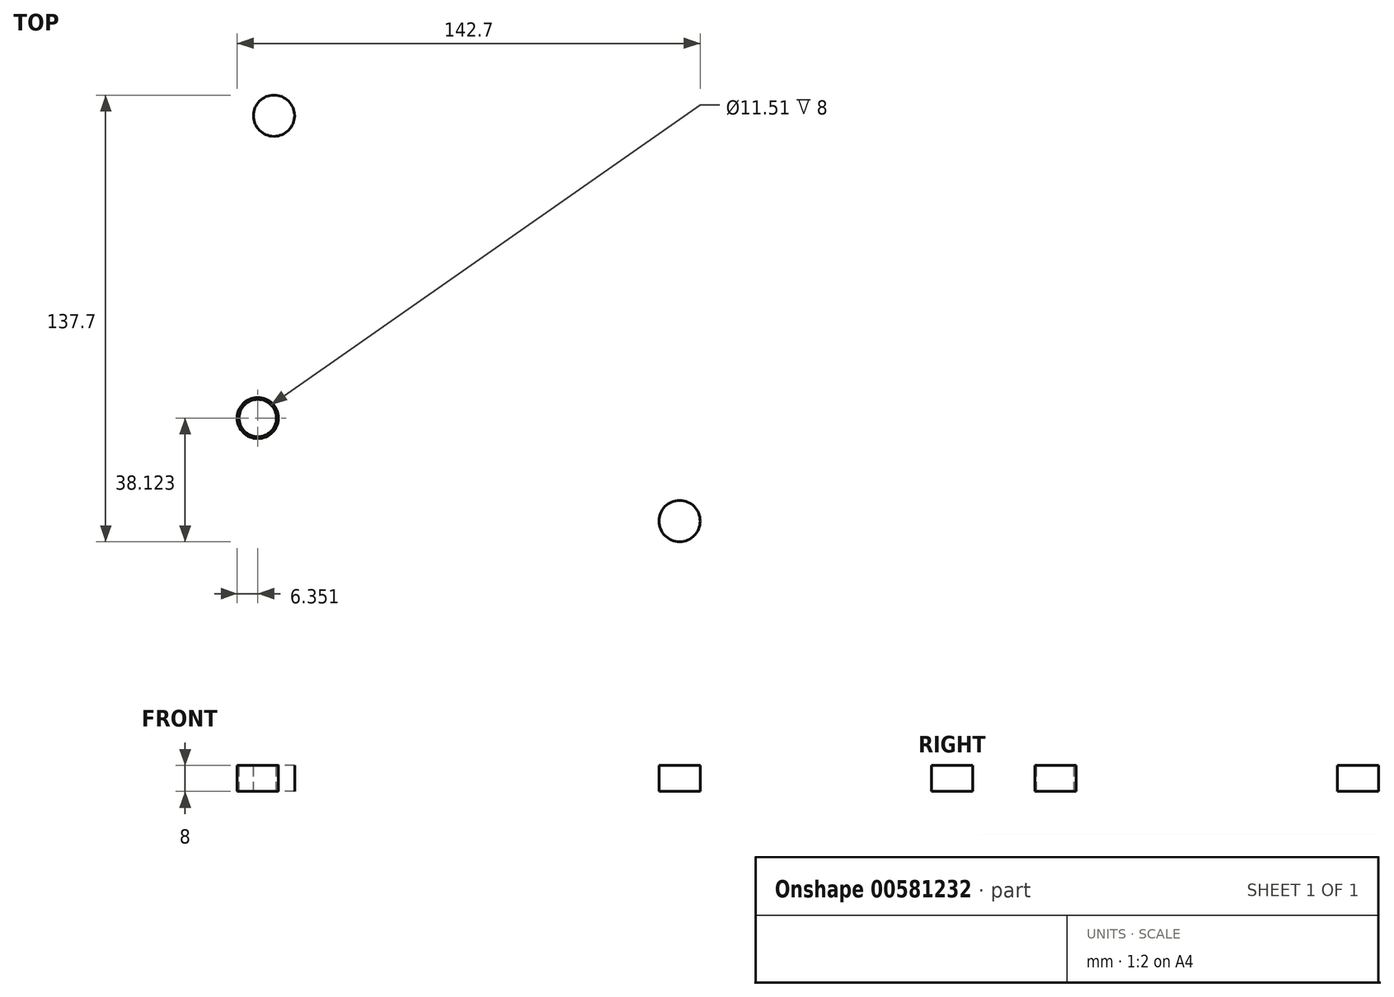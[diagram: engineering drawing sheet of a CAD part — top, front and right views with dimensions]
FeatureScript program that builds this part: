
annotation { "Feature Type Name" : "Feature", "Feature Type Description" : "" }
export const myFeature = defineFeature(function(context is Context, id is Id, definition is map)
    precondition{}
    {
        {
            var Q0;
            Q0=qCreatedBy(makeId("Top.planeOp"),FACE);
            var sketch = newSketch(context, id + "F0", { "sketchPlane" : qUnion([Q0])});
            skLineSegment(sketch, "E0.bottom", {"start": v(-93.63, 124.58) * mm, "end": v(31.37, 124.58) * mm});
            skLineSegment(sketch, "E0.top", {"start": v(-93.63, -40.42) * mm, "end": v(31.37, -40.42) * mm});
            skLineSegment(sketch, "E0.left", {"start": v(-113.63, 104.58) * mm, "end": v(-113.63, -20.42) * mm});
            skLineSegment(sketch, "E0.right", {"start": v(51.37, 104.58) * mm, "end": v(51.37, -20.42) * mm});
            skPoint(sketch, "E1.visualSharp", {"position": v(-113.63, 124.58) * mm});
            skArc(sketch, "E1.filletArc", {"start": v(-93.63, 124.58) * mm, "mid": v(-107.77, 118.73) * mm, "end": v(-113.63, 104.58) * mm});
            skPoint(sketch, "E2.visualSharp", {"position": v(51.37, 124.58) * mm});
            skArc(sketch, "E2.filletArc", {"start": v(51.37, 104.58) * mm, "mid": v(45.51, 118.73) * mm, "end": v(31.37, 124.58) * mm});
            skPoint(sketch, "E3.visualSharp", {"position": v(51.37, -40.42) * mm});
            skArc(sketch, "E3.filletArc", {"start": v(31.37, -40.42) * mm, "mid": v(45.51, -34.56) * mm, "end": v(51.37, -20.42) * mm});
            skPoint(sketch, "E4.visualSharp", {"position": v(-113.63, -40.42) * mm});
            skArc(sketch, "E4.filletArc", {"start": v(-113.63, -20.42) * mm, "mid": v(-107.77, -34.56) * mm, "end": v(-93.63, -40.42) * mm});
            skLineSegment(sketch, "E5.0", {"start": v(-68.63, 94.58) * mm, "end": v(6.37, 94.58) * mm});
            skLineSegment(sketch, "E5.1", {"start": v(-83.63, 79.58) * mm, "end": v(-83.63, 4.58) * mm});
            skLineSegment(sketch, "E5.2", {"start": v(-68.63, -10.42) * mm, "end": v(6.37, -10.42) * mm});
            skLineSegment(sketch, "E5.3", {"start": v(21.37, 79.58) * mm, "end": v(21.37, 4.58) * mm});
            skPoint(sketch, "E6.visualSharp", {"position": v(21.37, 94.58) * mm});
            skArc(sketch, "E6.filletArc", {"start": v(21.37, 79.58) * mm, "mid": v(16.98, 90.2) * mm, "end": v(6.37, 94.58) * mm});
            skPoint(sketch, "E7.visualSharp", {"position": v(21.37, -10.42) * mm});
            skArc(sketch, "E7.filletArc", {"start": v(6.37, -10.42) * mm, "mid": v(16.98, -6.02) * mm, "end": v(21.37, 4.58) * mm});
            skPoint(sketch, "E8.visualSharp", {"position": v(-83.63, -10.42) * mm});
            skArc(sketch, "E8.filletArc", {"start": v(-83.63, 4.58) * mm, "mid": v(-79.24, -6.02) * mm, "end": v(-68.63, -10.42) * mm});
            skPoint(sketch, "E9.visualSharp", {"position": v(-83.63, 94.58) * mm});
            skArc(sketch, "E9.filletArc", {"start": v(-68.63, 94.58) * mm, "mid": v(-79.24, 90.2) * mm, "end": v(-83.63, 79.58) * mm});
            skSolve(sketch);
        }
        {
            var Q0;
            Q0=makeQuery(id+"F0.imprint","IMPRINT",FACE,{"disambiguationData":[TD([[makeQuery(id+"F0.imprint","IMPRINT",EDGE,{"derivedFrom":sQuery(id+"F0.wireOp",EDGE,"E0.bottom")}),-1.0]])]});
            extrude(context, id + "F1", {"entities" : qUnion([Q0]), "depth" : 8 * mm, "offsetDistance" : 25 * mm});
        }
        {
            var Q0;
            Q0=makeQuery(id+"F1.opExtrude","CAP_FACE",FACE,{"disambiguationData":[OSD([sQuery(id+"F0.wireOp",EDGE,"E0.bottom"),sQuery(id+"F0.wireOp",EDGE,"E0.top"),sQuery(id+"F0.wireOp",EDGE,"E0.left"),sQuery(id+"F0.wireOp",EDGE,"E0.right"),sQuery(id+"F0.wireOp",EDGE,"E1.filletArc"),sQuery(id+"F0.wireOp",EDGE,"E2.filletArc"),sQuery(id+"F0.wireOp",EDGE,"E3.filletArc"),sQuery(id+"F0.wireOp",EDGE,"E4.filletArc"),sQuery(id+"F0.wireOp",EDGE,"E5.0"),sQuery(id+"F0.wireOp",EDGE,"E5.1"),sQuery(id+"F0.wireOp",EDGE,"E5.2"),sQuery(id+"F0.wireOp",EDGE,"E5.3"),sQuery(id+"F0.wireOp",EDGE,"E6.filletArc"),sQuery(id+"F0.wireOp",EDGE,"E7.filletArc"),sQuery(id+"F0.wireOp",EDGE,"E8.filletArc"),sQuery(id+"F0.wireOp",EDGE,"E9.filletArc")])],"isStart":false});
            var sketch = newSketch(context, id + "F2", { "sketchPlane" : qUnion([Q0])});
            skLineSegment(sketch, "E10", {"start": v(-113.63, 42.08) * mm, "end": v(-83.63, 42.08) * mm, "construction": true});
            skLineSegment(sketch, "E11", {"start": v(-31.13, 124.58) * mm, "end": v(-31.13, 94.58) * mm, "construction": true});
            skLineSegment(sketch, "E12", {"start": v(21.37, 42.08) * mm, "end": v(51.37, 42.08) * mm, "construction": true});
            skLineSegment(sketch, "E13", {"start": v(-31.13, -10.42) * mm, "end": v(-31.13, -40.42) * mm, "construction": true});
            skLineSegment(sketch, "E14", {"start": v(-31.13, -25.42) * mm, "end": v(85, -25.42) * mm, "construction": true});
            skLineSegment(sketch, "E15", {"start": v(-31.13, -25.42) * mm, "end": v(-152.16, -25.42) * mm, "construction": true});
            skLineSegment(sketch, "E16", {"start": v(-31.13, 109.58) * mm, "end": v(69.21, 109.58) * mm, "construction": true});
            skLineSegment(sketch, "E17", {"start": v(-31.13, 109.58) * mm, "end": v(-134.7, 109.58) * mm, "construction": true});
            skLineSegment(sketch, "E18", {"start": v(-98.63, 42.08) * mm, "end": v(-98.63, 145.3) * mm, "construction": true});
            skLineSegment(sketch, "E19", {"start": v(36.37, 42.08) * mm, "end": v(36.37, 143.63) * mm, "construction": true});
            skLineSegment(sketch, "E20", {"start": v(36.37, 42.08) * mm, "end": v(36.37, -62.39) * mm, "construction": true});
            skLineSegment(sketch, "E21", {"start": v(-98.63, 42.08) * mm, "end": v(-98.63, -55.69) * mm, "construction": true});
            skCircle(sketch, "E22", {"center": v(-31.13, 109.58) * mm, "radius": 6.35 * mm});
            skCircle(sketch, "E23", {"center": v(-31.13, -25.42) * mm, "radius": 6.35 * mm});
            skCircle(sketch, "E24", {"center": v(-98.63, 42.08) * mm, "radius": 6.35 * mm});
            skCircle(sketch, "E25", {"center": v(36.37, 42.08) * mm, "radius": 6.35 * mm});
            skCircle(sketch, "E26", {"center": v(31.37, 104.58) * mm, "radius": 6.35 * mm});
            skCircle(sketch, "E27.MirrorC", {"center": v(31.37, -20.42) * mm, "radius": 6.35 * mm});
            skCircle(sketch, "E28.MirrorC", {"center": v(-93.63, 104.58) * mm, "radius": 6.35 * mm});
            skCircle(sketch, "E29.MirrorC", {"center": v(-93.63, -20.42) * mm, "radius": 6.35 * mm});
            skCircle(sketch, "E30", {"center": v(-98.63, 11.35) * mm, "radius": 6.35 * mm});
            skSolve(sketch);
        }
        {
            var Q0;
            Q0=makeQuery(id+"F2.imprint","IMPRINT",FACE,{"disambiguationData":[TD([[makeQuery(id+"F2.imprint","IMPRINT",EDGE,{"derivedFrom":sQuery(id+"F2.wireOp",EDGE,"E28.MirrorC")}),-1.0]])]});
            var Q1;
            Q1=makeQuery(id+"F2.imprint","IMPRINT",FACE,{"disambiguationData":[TD([[makeQuery(id+"F2.imprint","IMPRINT",EDGE,{"derivedFrom":sQuery(id+"F2.wireOp",EDGE,"E22")}),1.0]])]});
            var Q2;
            Q2=makeQuery(id+"F2.imprint","IMPRINT",FACE,{"disambiguationData":[TD([[makeQuery(id+"F2.imprint","IMPRINT",EDGE,{"derivedFrom":sQuery(id+"F2.wireOp",EDGE,"E26")}),1.0]])]});
            var Q3;
            Q3=makeQuery(id+"F2.imprint","IMPRINT",FACE,{"disambiguationData":[TD([[makeQuery(id+"F2.imprint","IMPRINT",EDGE,{"derivedFrom":sQuery(id+"F2.wireOp",EDGE,"E25")}),1.0]])]});
            var Q4;
            Q4=makeQuery(id+"F2.imprint","IMPRINT",FACE,{"disambiguationData":[TD([[makeQuery(id+"F2.imprint","IMPRINT",EDGE,{"derivedFrom":sQuery(id+"F2.wireOp",EDGE,"E27.MirrorC")}),-1.0]])]});
            var Q5;
            Q5=makeQuery(id+"F2.imprint","IMPRINT",FACE,{"disambiguationData":[TD([[makeQuery(id+"F2.imprint","IMPRINT",EDGE,{"derivedFrom":sQuery(id+"F2.wireOp",EDGE,"E23")}),1.0]])]});
            var Q6;
            Q6=makeQuery(id+"F2.imprint","IMPRINT",FACE,{"disambiguationData":[TD([[makeQuery(id+"F2.imprint","IMPRINT",EDGE,{"derivedFrom":sQuery(id+"F2.wireOp",EDGE,"E29.MirrorC")}),1.0]])]});
            var Q7;
            Q7=makeQuery(id+"F2.imprint","IMPRINT",FACE,{"disambiguationData":[TD([[makeQuery(id+"F2.imprint","IMPRINT",EDGE,{"derivedFrom":sQuery(id+"F2.wireOp",EDGE,"E24")}),1.0]])]});
            extrude(context, id + "F3", {"entities" : qUnion([Q0, Q1, Q2, Q3, Q4, Q5, Q6, Q7]), "operationType" : NewBodyOperationType.REMOVE, "endBound" : BoundingType.THROUGH_ALL, "oppositeDirection" : true, "depth" : 25 * mm, "offsetDistance" : 25 * mm});
        }
        {
            var Q0;
            Q0=sQuery(id+"F2.wireOp",VERTEX,"E30.center");
            var Q1;
            Q1=makeQuery(id+"F1.opExtrude","SWEPT_BODY",BODY,{"disambiguationData":[OSD([sQuery(id+"F0.wireOp",EDGE,"E0.bottom"),sQuery(id+"F0.wireOp",EDGE,"E0.top"),sQuery(id+"F0.wireOp",EDGE,"E0.left"),sQuery(id+"F0.wireOp",EDGE,"E0.right"),sQuery(id+"F0.wireOp",EDGE,"E1.filletArc"),sQuery(id+"F0.wireOp",EDGE,"E2.filletArc"),sQuery(id+"F0.wireOp",EDGE,"E3.filletArc"),sQuery(id+"F0.wireOp",EDGE,"E4.filletArc"),sQuery(id+"F0.wireOp",EDGE,"E5.0"),sQuery(id+"F0.wireOp",EDGE,"E5.1"),sQuery(id+"F0.wireOp",EDGE,"E5.2"),sQuery(id+"F0.wireOp",EDGE,"E5.3"),sQuery(id+"F0.wireOp",EDGE,"E6.filletArc"),sQuery(id+"F0.wireOp",EDGE,"E7.filletArc"),sQuery(id+"F0.wireOp",EDGE,"E8.filletArc"),sQuery(id+"F0.wireOp",EDGE,"E9.filletArc")])]});
            hole(context, id + "F4", {"style" : HoleStyle.SIMPLE, "endStyle" : HoleEndStyle.THROUGH, "standardTappedOrClearance" : lookupTablePath({ "standard" : "ANSI", "engagement" : "75%", "pitch" : "20 tpi", "size" : "1/2", "type" : "Tapped" }), "standardBlindInLast" : lookupTablePath({ "standard" : "ANSI", "engagement" : "75%", "pitch" : "20 tpi", "size" : "1/2", "type" : "Tapped" }), "holeDiameter" : 11.5 * mm, "majorDiameter" : 12.7 * mm, "showTappedDepth" : true, "isTappedThrough" : true, "tappedDepth" : 12 * mm, "tapClearance" : 3, "locations" : qUnion([Q0]), "scope" : qUnion([Q1])});
        }
    });
